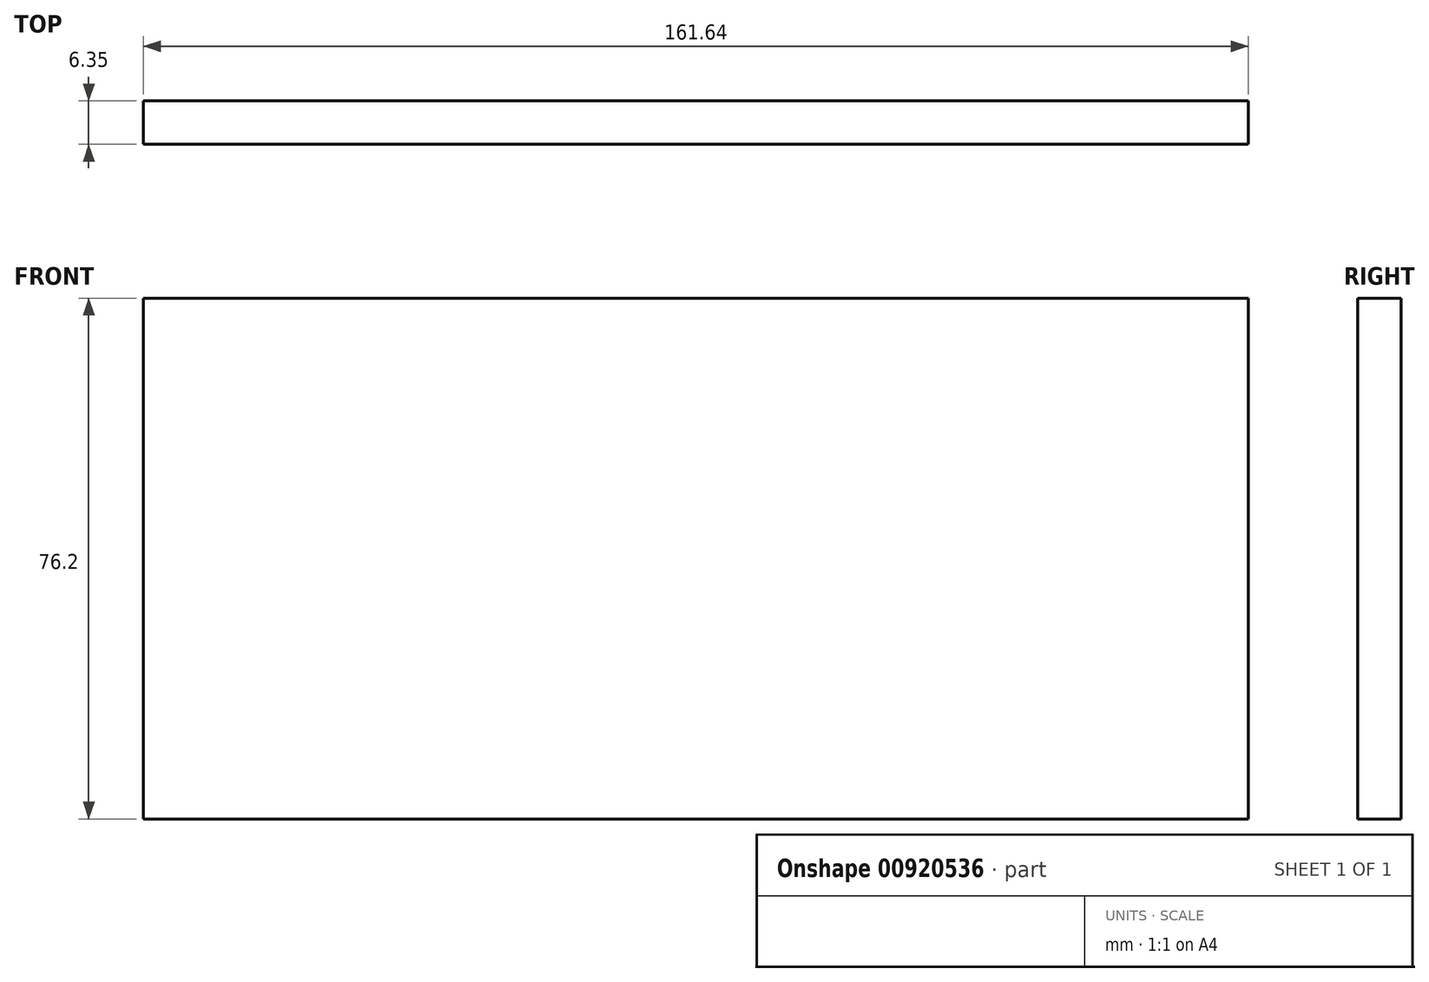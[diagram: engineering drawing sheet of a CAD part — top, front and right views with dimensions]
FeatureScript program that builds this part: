
annotation { "Feature Type Name" : "Feature", "Feature Type Description" : "" }
export const myFeature = defineFeature(function(context is Context, id is Id, definition is map)
    precondition{}
    {
        {
            var Q0;
            Q0=qCreatedBy(makeId("Front.planeOp"),FACE);
            var sketch = newSketch(context, id + "F0", { "sketchPlane" : qUnion([Q0])});
            skLineSegment(sketch, "E0.bottom", {"start": v(0, 38.1) * mm, "end": v(161.64, 38.1) * mm});
            skLineSegment(sketch, "E0.top", {"start": v(0, -38.1) * mm, "end": v(161.64, -38.1) * mm});
            skLineSegment(sketch, "E0.left", {"start": v(0, 38.1) * mm, "end": v(0, -38.1) * mm});
            skLineSegment(sketch, "E0.right", {"start": v(161.64, 38.1) * mm, "end": v(161.64, -38.1) * mm});
            skSolve(sketch);
        }
        {
            var Q0;
            Q0=makeQuery(id+"F0.imprint","IMPRINT",FACE,{"disambiguationData":[TD([[makeQuery(id+"F0.imprint","IMPRINT",EDGE,{"derivedFrom":sQuery(id+"F0.wireOp",EDGE,"E0.bottom")}),-1.0]])]});
            extrude(context, id + "F1", {"entities" : qUnion([Q0]), "oppositeDirection" : true, "depth" : 6.35 * mm, "offsetDistance" : 25.4 * mm});
        }
    });
